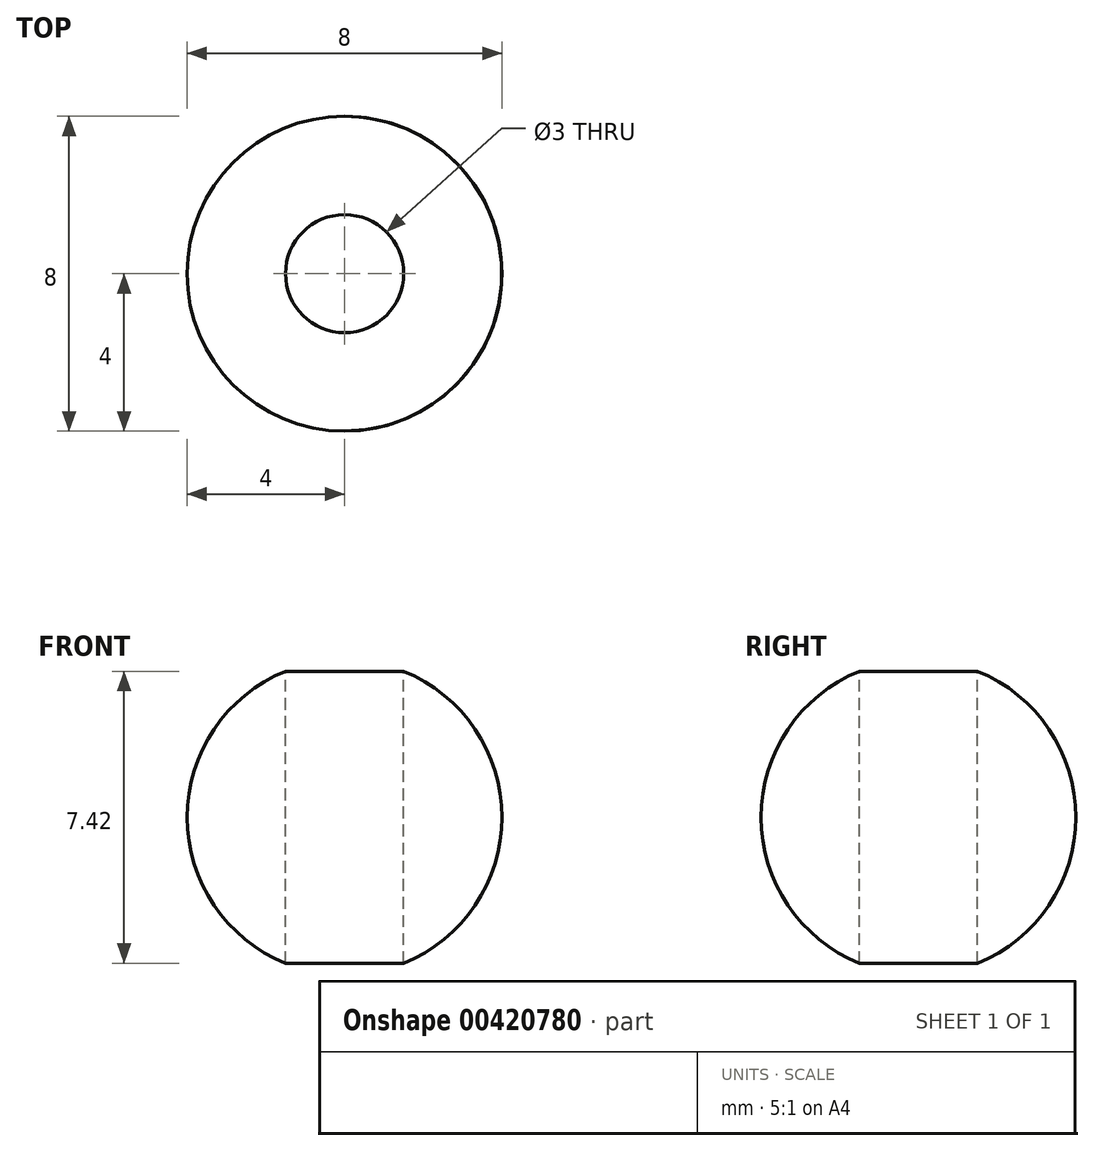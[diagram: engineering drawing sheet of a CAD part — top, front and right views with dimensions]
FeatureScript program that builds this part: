
annotation { "Feature Type Name" : "Feature", "Feature Type Description" : "" }
export const myFeature = defineFeature(function(context is Context, id is Id, definition is map)
    precondition{}
    {
        {
            var Q0;
            Q0=qCreatedBy(makeId("Top.planeOp"),FACE);
            var sketch = newSketch(context, id + "F0", { "sketchPlane" : qUnion([Q0])});
            skCircle(sketch, "E0", {"center": v(0, 0) * mm, "radius": 4 * mm});
            skLineSegment(sketch, "E1", {"start": v(0, 4) * mm, "end": v(0, -4) * mm});
            skCircle(sketch, "E2", {"center": v(0, 0) * mm, "radius": 1.5 * mm});
            skSolve(sketch);
        }
        {
            var Q0;
            {var subQ0=sQuery(id+"F0.wireOp",EDGE,"E1");Q0=makeQuery(id+"F0.imprint","IMPRINT",FACE,{"disambiguationData":[TD([[makeQuery(id+"F0.imprint","IMPRINT",EDGE,{"derivedFrom":subQ0}),1.0]])]});}
            var Q1;
            Q1=sQuery(id+"F0.wireOp",EDGE,"E1");
            revolve(context, id + "F1", {"entities" : qUnion([Q0]), "axis" : qUnion([Q1]), "revolveType" : RevolveType.FULL});
        }
        {
            var Q0;
            {var subQ0=sQuery(id+"F0.wireOp",EDGE,"E2");var subQ1=sQuery(id+"F0.wireOp",EDGE,"E1");var subQ2=makeQuery(id+"F0.imprint","INTERSECT",VERTEX,{"disambiguationData":[OD(0.0)],"derivedFrom":[subQ1,subQ0]});Q0=makeQuery(id+"F0.imprint","IMPRINT",FACE,{"disambiguationData":[TD([[makeQuery(id+"F0.imprint","IMPRINT",EDGE,{"disambiguationData":[TD([[subQ2,-1.0]])],"derivedFrom":subQ1}),-1.0]])]});}
            var Q1;
            {var subQ0=sQuery(id+"F0.wireOp",EDGE,"E2");var subQ1=sQuery(id+"F0.wireOp",EDGE,"E1");var subQ2=makeQuery(id+"F0.imprint","INTERSECT",VERTEX,{"disambiguationData":[OD(0.0)],"derivedFrom":[subQ1,subQ0]});Q1=makeQuery(id+"F0.imprint","IMPRINT",FACE,{"disambiguationData":[TD([[makeQuery(id+"F0.imprint","IMPRINT",EDGE,{"disambiguationData":[TD([[subQ2,-1.0]])],"derivedFrom":subQ1}),1.0]])]});}
            extrude(context, id + "F2", {"entities" : qUnion([Q0, Q1]), "operationType" : NewBodyOperationType.REMOVE, "endBound" : BoundingType.SYMMETRIC, "oppositeDirection" : true, "depth" : 10 * mm});
        }
    });
